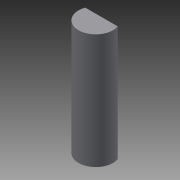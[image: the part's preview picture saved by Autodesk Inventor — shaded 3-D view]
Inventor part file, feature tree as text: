
AUTODESK INVENTOR PART (.ipt)
format: ipt  version: 2014 (Build 180170000, 170)  size: 68,096 bytes
history: native  units: mm
features: extrude x1, sketch x1
ambient origin geometry x8: Origin, YZ Plane, XZ Plane, XY Plane, X Axis, Y Axis, Z Axis, Center Point
bodies: Volumenkörper1 (feature_tree)
feature tree (2):
  extrude  "Extrusion1"  Depth=10.0mm
  sketch  "Skizze1"  dims[d0=3.0mm d1=1.0mm d2=10.0mm d3=0.0mm]
